# Revit family: RUFO2 360xWSxZ0250xx
name_source: partatom
category: Leuchten
units: mm (PartAtom-declared; Revit-internal decimal feet)

## family parameters
Basisbauteil = Fläche
Beim Laden mit Abzugskörper schneiden = Nein
Bemaßung runder Anschluss = Durchmesser verwenden
Gemeinsam genutzt = Nein
Lichtquelle = Ja
OmniClass-Nummer = 23.80.70.11
OmniClass-Titel = Luminaries for Internal Lighting
Raumberechnungspunkt = Nein
Teiletyp = Normal

## types (18) — shared parameters
Baugruppenkennzeichen = D5020200
Datei für fotometrisches Netz = RUFO2_360_Z.IES
Emissionsform beim Rendern sichtbar = Nein
Farbfilter = 16777215
Farbtemperaturverschiebung bei Dämpfen der Lampe = <Keine Auswahl>
Hersteller = RIDI Leuchten GmbH
Lampe = LED
Neigungswinkel = 90.00°
Scheinlast = 17 VA
URL = www.ridi.de
Von Kreisdurchmesser aussenden = 360 mm  [stored 1.1811 ft]
brand = RIDI
conformity mark = CE
electrical safety class = 1
height = 70 mm  [stored 0.229659 ft]
ingress protection (IP) code = IP40
length = 360 mm  [stored 1.1811 ft]
nominal frequency = 50-60Hz
nominal voltage = 230
rated input power = 17
voltage type (AC, DC, UC) = AC
width = 360 mm  [stored 1.1811 ft]
zero-valued in all types: Vorgabe-Ansicht

## per-type parameters (varying)
| type | Modell | weight |
| RUFO2 360NDWS840Z0250 | 0420867 | 1,4 kg |
| RUFO2 360NDWS840Z0250-RS | 0420867//396 | 1,45 kg |
| RUFO2 360NDWS840Z0250-2K | 0420868 | 1,5 kg |
| RUFO2 360NDWS830Z0250 | 0420873 | 1,4 kg |
| RUFO2 360NDWS830Z0250-RS | 0420873//396 | 1,45 kg |
| RUFO2 360NDWS830Z0250-2K | 0420874 | 1,5 kg |
| RUFO2 360NDWS840Z0250-IK | 0420879 | 1,4 kg |
| RUFO2 360NDWS840Z0250-IK-EDS3 | 0420879//377 | 1,26 kg |
| RUFO2 360NDWS840Z0250-IK-RS | 0420879//396 | 1,45 kg |
| RUFO2 360NDWS840Z0250-IK-2K | 0420880 | 1,5 kg |
| RUFO2 360NDWS830Z0250-IK | 0420885 | 1,4 kg |
| RUFO2 360NDWS830Z0250-IK-EDS3 | 0420885//377 | 1,26 kg |
| RUFO2 360NDWS830Z0250-IK-RS | 0420885//396 | 1,45 kg |
| RUFO2 360NDWS830Z0250-IK-2K | 0420886 | 1,5 kg |
| RUFO2 360DAWS840Z0250 | 0430867 | 1,45 kg |
| RUFO2 360DAWS830Z0250 | 0430873 | 1,45 kg |
| RUFO2 360DAWS840Z0250-IK | 0430879 | 1,45 kg |
| RUFO2 360DAWS830Z0250-IK | 0430885 | 1,45 kg |

note: column(s) folded — value = type name in every type: product name

note: [stored X ft] marks values corroborated as IEEE doubles in the binary element streams (Revit-internal decimal feet)
